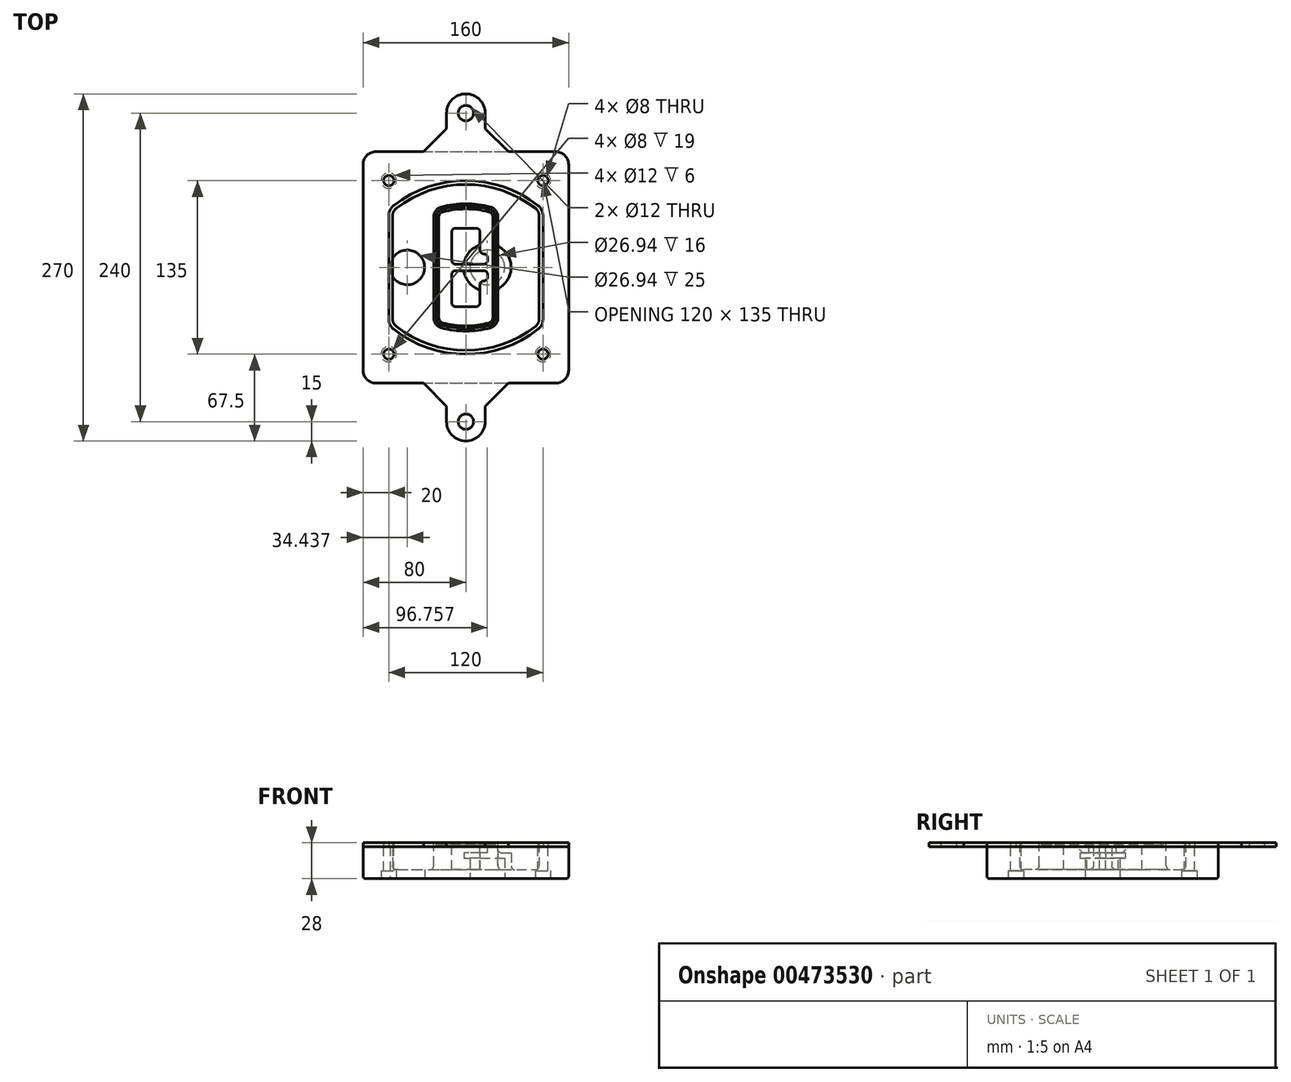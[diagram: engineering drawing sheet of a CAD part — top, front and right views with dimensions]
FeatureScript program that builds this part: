
annotation { "Feature Type Name" : "Feature", "Feature Type Description" : "" }
export const myFeature = defineFeature(function(context is Context, id is Id, definition is map)
    precondition{}
    {
        {
            var Q0;
            Q0=qCreatedBy(makeId("Top.planeOp"),FACE);
            var sketch = newSketch(context, id + "F0", { "sketchPlane" : qUnion([Q0])});
            skPoint(sketch, "E0.rect.middle", {"position": v(0, 0) * mm});
            skLineSegment(sketch, "E1.bottom", {"start": v(-70, -90) * mm, "end": v(70, -90) * mm});
            skLineSegment(sketch, "E1.top", {"start": v(-70, 90) * mm, "end": v(70, 90) * mm});
            skLineSegment(sketch, "E1.left", {"start": v(-80, -80) * mm, "end": v(-80, 80) * mm});
            skLineSegment(sketch, "E1.right", {"start": v(80, -80) * mm, "end": v(80, 80) * mm});
            skLineSegment(sketch, "E2", {"start": v(-80, 90) * mm, "end": v(80, -90) * mm, "construction": true});
            skLineSegment(sketch, "E3", {"start": v(80, 90) * mm, "end": v(-80, -90) * mm, "construction": true});
            skCircle(sketch, "E4", {"center": v(-60, 67.5) * mm, "radius": 4 * mm});
            skCircle(sketch, "E5", {"center": v(60, 67.5) * mm, "radius": 4 * mm});
            skCircle(sketch, "E6", {"center": v(60, -67.5) * mm, "radius": 4 * mm});
            skCircle(sketch, "E7", {"center": v(-60, -67.5) * mm, "radius": 4 * mm});
            skLineSegment(sketch, "E8", {"start": v(-60, 67.5) * mm, "end": v(60, 67.5) * mm, "construction": true});
            skLineSegment(sketch, "E9", {"start": v(60, 67.5) * mm, "end": v(60, -67.5) * mm, "construction": true});
            skLineSegment(sketch, "E10", {"start": v(60, -67.5) * mm, "end": v(-60, -67.5) * mm, "construction": true});
            skLineSegment(sketch, "E11", {"start": v(-60, -67.5) * mm, "end": v(-60, 67.5) * mm, "construction": true});
            skLineSegment(sketch, "E12", {"start": v(-60, 40.3) * mm, "end": v(-60, -40.3) * mm});
            skLineSegment(sketch, "E13", {"start": v(60, 40.3) * mm, "end": v(60, -40.3) * mm});
            skArc(sketch, "E14", {"start": v(56.15, 48.18) * mm, "mid": v(0, 67.5) * mm, "end": v(-56.15, 48.18) * mm});
            skArc(sketch, "E15", {"start": v(-56.15, -48.18) * mm, "mid": v(0, -67.5) * mm, "end": v(56.15, -48.18) * mm});
            skLineSegment(sketch, "E16", {"start": v(-60, 0) * mm, "end": v(60, 0) * mm, "construction": true});
            skPoint(sketch, "E17.visualSharp", {"position": v(-60, -45) * mm});
            skArc(sketch, "E17.filletArc", {"start": v(-60, -40.3) * mm, "mid": v(-58.99, -44.68) * mm, "end": v(-56.15, -48.18) * mm});
            skPoint(sketch, "E18.visualSharp", {"position": v(-60, 45) * mm});
            skArc(sketch, "E18.filletArc", {"start": v(-56.15, 48.18) * mm, "mid": v(-58.99, 44.68) * mm, "end": v(-60, 40.3) * mm});
            skPoint(sketch, "E19.visualSharp", {"position": v(60, 45) * mm});
            skArc(sketch, "E19.filletArc", {"start": v(60, 40.3) * mm, "mid": v(58.99, 44.68) * mm, "end": v(56.15, 48.18) * mm});
            skPoint(sketch, "E20.visualSharp", {"position": v(60, -45) * mm});
            skArc(sketch, "E20.filletArc", {"start": v(56.15, -48.18) * mm, "mid": v(58.99, -44.68) * mm, "end": v(60, -40.3) * mm});
            skPoint(sketch, "E21.visualSharp", {"position": v(-80, 90) * mm});
            skArc(sketch, "E21.filletArc", {"start": v(-70, 90) * mm, "mid": v(-77.07, 87.07) * mm, "end": v(-80, 80) * mm});
            skPoint(sketch, "E22.visualSharp", {"position": v(80, 90) * mm});
            skArc(sketch, "E22.filletArc", {"start": v(80, 80) * mm, "mid": v(77.07, 87.07) * mm, "end": v(70, 90) * mm});
            skPoint(sketch, "E23.visualSharp", {"position": v(80, -90) * mm});
            skArc(sketch, "E23.filletArc", {"start": v(70, -90) * mm, "mid": v(77.07, -87.07) * mm, "end": v(80, -80) * mm});
            skPoint(sketch, "E24.visualSharp", {"position": v(-80, -90) * mm});
            skArc(sketch, "E24.filletArc", {"start": v(-80, -80) * mm, "mid": v(-77.07, -87.07) * mm, "end": v(-70, -90) * mm});
            skArc(sketch, "E25.0", {"start": v(57, 40.3) * mm, "mid": v(56.3, 43.36) * mm, "end": v(54.3, 45.81) * mm});
            skLineSegment(sketch, "E25.1", {"start": v(57, 40.3) * mm, "end": v(57, -40.3) * mm});
            skArc(sketch, "E25.2", {"start": v(54.3, -45.81) * mm, "mid": v(56.3, -43.36) * mm, "end": v(57, -40.3) * mm});
            skArc(sketch, "E25.3", {"start": v(-54.3, -45.81) * mm, "mid": v(0, -64.5) * mm, "end": v(54.3, -45.81) * mm});
            skArc(sketch, "E25.4", {"start": v(-57, -40.3) * mm, "mid": v(-56.3, -43.36) * mm, "end": v(-54.3, -45.81) * mm});
            skArc(sketch, "E25.5", {"start": v(54.3, 45.81) * mm, "mid": v(0, 64.5) * mm, "end": v(-54.3, 45.81) * mm});
            skLineSegment(sketch, "E25.6", {"start": v(-57, 40.3) * mm, "end": v(-57, -40.3) * mm});
            skArc(sketch, "E25.7", {"start": v(-54.3, 45.81) * mm, "mid": v(-56.3, 43.36) * mm, "end": v(-57, 40.3) * mm});
            skArc(sketch, "E26.0", {"start": v(-58.62, 51.33) * mm, "mid": v(-62.58, 46.43) * mm, "end": v(-64, 40.3) * mm});
            skArc(sketch, "E26.1", {"start": v(58.62, 51.33) * mm, "mid": v(0, 71.5) * mm, "end": v(-58.62, 51.33) * mm});
            skArc(sketch, "E26.2", {"start": v(64, 40.3) * mm, "mid": v(62.58, 46.43) * mm, "end": v(58.62, 51.33) * mm});
            skLineSegment(sketch, "E26.3", {"start": v(64, 40.3) * mm, "end": v(64, -40.3) * mm});
            skArc(sketch, "E26.4", {"start": v(58.62, -51.33) * mm, "mid": v(62.58, -46.43) * mm, "end": v(64, -40.3) * mm});
            skLineSegment(sketch, "E26.5", {"start": v(-64, 40.3) * mm, "end": v(-64, -40.3) * mm});
            skArc(sketch, "E26.6", {"start": v(-58.62, -51.33) * mm, "mid": v(0, -71.5) * mm, "end": v(58.62, -51.33) * mm});
            skArc(sketch, "E26.7", {"start": v(-64, -40.3) * mm, "mid": v(-62.58, -46.43) * mm, "end": v(-58.62, -51.33) * mm});
            skSolve(sketch);
        }
        {
            var Q0;
            Q0=makeQuery(id+"F0.imprint","IMPRINT",FACE,{"disambiguationData":[TD([[makeQuery(id+"F0.imprint","IMPRINT",EDGE,{"derivedFrom":sQuery(id+"F0.wireOp",EDGE,"E1.bottom")}),1.0]])]});
            var Q1;
            Q1=makeQuery(id+"F0.imprint","IMPRINT",FACE,{"disambiguationData":[TD([[makeQuery(id+"F0.imprint","IMPRINT",EDGE,{"derivedFrom":sQuery(id+"F0.wireOp",EDGE,"E12")}),1.0]])]});
            var Q2;
            Q2=makeQuery(id+"F0.imprint","IMPRINT",FACE,{"disambiguationData":[TD([[makeQuery(id+"F0.imprint","IMPRINT",EDGE,{"derivedFrom":sQuery(id+"F0.wireOp",EDGE,"E25.0")}),1.0]])]});
            var Q3;
            Q3=makeQuery(id+"F0.imprint","IMPRINT",FACE,{"disambiguationData":[TD([[makeQuery(id+"F0.imprint","IMPRINT",EDGE,{"derivedFrom":sQuery(id+"F0.wireOp",EDGE,"E12")}),-1.0]])]});
            extrude(context, id + "F1", {"entities" : qUnion([Q0, Q1, Q2, Q3]), "oppositeDirection" : true, "depth" : 25 * mm});
        }
        {
            var Q0;
            Q0=makeQuery(id+"F0.imprint","IMPRINT",FACE,{"disambiguationData":[TD([[makeQuery(id+"F0.imprint","IMPRINT",EDGE,{"derivedFrom":sQuery(id+"F0.wireOp",EDGE,"E12")}),1.0]])]});
            extrude(context, id + "F2", {"entities" : qUnion([Q0]), "operationType" : NewBodyOperationType.ADD, "depth" : 3 * mm});
        }
        {
            var Q0;
            Q0=makeQuery(id+"F0.imprint","IMPRINT",FACE,{"disambiguationData":[TD([[makeQuery(id+"F0.imprint","IMPRINT",EDGE,{"derivedFrom":sQuery(id+"F0.wireOp",EDGE,"E25.0")}),1.0]])]});
            extrude(context, id + "F3", {"entities" : qUnion([Q0]), "operationType" : NewBodyOperationType.REMOVE, "oppositeDirection" : true, "depth" : 18 * mm});
        }
        {
            var Q0;
            Q0=makeQuery(id+"F2.opExtrude","CAP_FACE",FACE,{"disambiguationData":[OSD([sQuery(id+"F0.wireOp",EDGE,"E12"),sQuery(id+"F0.wireOp",EDGE,"E13"),sQuery(id+"F0.wireOp",EDGE,"E14"),sQuery(id+"F0.wireOp",EDGE,"E15"),sQuery(id+"F0.wireOp",EDGE,"E17.filletArc"),sQuery(id+"F0.wireOp",EDGE,"E18.filletArc"),sQuery(id+"F0.wireOp",EDGE,"E19.filletArc"),sQuery(id+"F0.wireOp",EDGE,"E20.filletArc"),sQuery(id+"F0.wireOp",EDGE,"E25.0"),sQuery(id+"F0.wireOp",EDGE,"E25.1"),sQuery(id+"F0.wireOp",EDGE,"E25.2"),sQuery(id+"F0.wireOp",EDGE,"E25.3"),sQuery(id+"F0.wireOp",EDGE,"E25.4"),sQuery(id+"F0.wireOp",EDGE,"E25.5"),sQuery(id+"F0.wireOp",EDGE,"E25.6"),sQuery(id+"F0.wireOp",EDGE,"E25.7")])],"isStart":false});
            var sketch = newSketch(context, id + "F4", { "sketchPlane" : qUnion([Q0])});
            skArc(sketch, "E27.0", {"start": v(-19.08, -46.97) * mm, "mid": v(0, -49.5) * mm, "end": v(19.08, -46.97) * mm});
            skArc(sketch, "E28.0", {"start": v(19.08, 46.97) * mm, "mid": v(0, 49.5) * mm, "end": v(-19.08, 46.97) * mm});
            skLineSegment(sketch, "E29", {"start": v(-25, 39.25) * mm, "end": v(-25, -39.25) * mm});
            skLineSegment(sketch, "E30", {"start": v(25, 39.25) * mm, "end": v(25, -39.25) * mm});
            skLineSegment(sketch, "E31", {"start": v(-25, 45.1) * mm, "end": v(25, 45.1) * mm, "construction": true});
            skLineSegment(sketch, "E32", {"start": v(-25, -45.1) * mm, "end": v(25, -45.1) * mm, "construction": true});
            skPoint(sketch, "E33.visualSharp", {"position": v(-25, 45.1) * mm});
            skArc(sketch, "E33.filletArc", {"start": v(-19.08, 46.97) * mm, "mid": v(-23.35, 44.11) * mm, "end": v(-25, 39.25) * mm});
            skPoint(sketch, "E34.visualSharp", {"position": v(25, 45.1) * mm});
            skArc(sketch, "E34.filletArc", {"start": v(25, 39.25) * mm, "mid": v(23.35, 44.11) * mm, "end": v(19.08, 46.97) * mm});
            skPoint(sketch, "E35.visualSharp", {"position": v(25, -45.1) * mm});
            skArc(sketch, "E35.filletArc", {"start": v(19.08, -46.97) * mm, "mid": v(23.35, -44.11) * mm, "end": v(25, -39.25) * mm});
            skPoint(sketch, "E36.visualSharp", {"position": v(-25, -45.1) * mm});
            skArc(sketch, "E36.filletArc", {"start": v(-25, -39.25) * mm, "mid": v(-23.35, -44.11) * mm, "end": v(-19.08, -46.97) * mm});
            skArc(sketch, "E37.0", {"start": v(54.3, 45.81) * mm, "mid": v(0, 64.5) * mm, "end": v(-54.3, 45.81) * mm});
            skArc(sketch, "E37.1", {"start": v(-54.3, 45.81) * mm, "mid": v(-56.3, 43.36) * mm, "end": v(-57, 40.3) * mm});
            skLineSegment(sketch, "E37.2", {"start": v(-57, 40.3) * mm, "end": v(-57, -40.3) * mm});
            skArc(sketch, "E37.3", {"start": v(-57, -40.3) * mm, "mid": v(-56.3, -43.36) * mm, "end": v(-54.3, -45.81) * mm});
            skArc(sketch, "E37.4", {"start": v(-54.3, -45.81) * mm, "mid": v(0, -64.5) * mm, "end": v(54.3, -45.81) * mm});
            skArc(sketch, "E37.5", {"start": v(54.3, -45.81) * mm, "mid": v(56.3, -43.36) * mm, "end": v(57, -40.3) * mm});
            skLineSegment(sketch, "E37.6", {"start": v(57, 40.3) * mm, "end": v(57, -40.3) * mm});
            skArc(sketch, "E37.7", {"start": v(57, 40.3) * mm, "mid": v(56.3, 43.36) * mm, "end": v(54.3, 45.81) * mm});
            skLineSegment(sketch, "E38.0", {"start": v(23, 39.25) * mm, "end": v(23, -39.25) * mm});
            skArc(sketch, "E38.1", {"start": v(18.56, -45.04) * mm, "mid": v(21.76, -42.9) * mm, "end": v(23, -39.25) * mm});
            skArc(sketch, "E38.2", {"start": v(-18.56, -45.04) * mm, "mid": v(0, -47.5) * mm, "end": v(18.56, -45.04) * mm});
            skArc(sketch, "E38.3", {"start": v(-23, -39.25) * mm, "mid": v(-21.76, -42.9) * mm, "end": v(-18.56, -45.04) * mm});
            skLineSegment(sketch, "E38.4", {"start": v(-23, 39.25) * mm, "end": v(-23, -39.25) * mm});
            skArc(sketch, "E38.5", {"start": v(23, 39.25) * mm, "mid": v(21.76, 42.9) * mm, "end": v(18.56, 45.04) * mm});
            skArc(sketch, "E38.6", {"start": v(-18.56, 45.04) * mm, "mid": v(-21.76, 42.9) * mm, "end": v(-23, 39.25) * mm});
            skArc(sketch, "E38.7", {"start": v(18.56, 45.04) * mm, "mid": v(0, 47.5) * mm, "end": v(-18.56, 45.04) * mm});
            skArc(sketch, "E39.0", {"start": v(21, 39.25) * mm, "mid": v(20.18, 41.68) * mm, "end": v(18.04, 43.1) * mm});
            skLineSegment(sketch, "E39.1", {"start": v(21, 39.25) * mm, "end": v(21, -39.25) * mm});
            skArc(sketch, "E39.2", {"start": v(18.04, -43.1) * mm, "mid": v(20.18, -41.68) * mm, "end": v(21, -39.25) * mm});
            skArc(sketch, "E39.3", {"start": v(-18.04, -43.1) * mm, "mid": v(0, -45.5) * mm, "end": v(18.04, -43.1) * mm});
            skArc(sketch, "E39.4", {"start": v(-21, -39.25) * mm, "mid": v(-20.18, -41.68) * mm, "end": v(-18.04, -43.1) * mm});
            skArc(sketch, "E39.5", {"start": v(18.04, 43.1) * mm, "mid": v(0, 45.5) * mm, "end": v(-18.04, 43.1) * mm});
            skLineSegment(sketch, "E39.6", {"start": v(-21, 39.25) * mm, "end": v(-21, -39.25) * mm});
            skArc(sketch, "E39.7", {"start": v(-18.04, 43.1) * mm, "mid": v(-20.18, 41.68) * mm, "end": v(-21, 39.25) * mm});
            skLineSegment(sketch, "E40", {"start": v(-25, 0) * mm, "end": v(25, 0) * mm, "construction": true});
            skLineSegment(sketch, "E41", {"start": v(-11, 5.5) * mm, "end": v(-11, 27.5) * mm});
            skLineSegment(sketch, "E42", {"start": v(-8, 30.5) * mm, "end": v(8, 30.5) * mm});
            skLineSegment(sketch, "E43", {"start": v(11, 27.5) * mm, "end": v(11, 13.5) * mm});
            skLineSegment(sketch, "E44", {"start": v(14, 10.5) * mm, "end": v(14, 10.5) * mm});
            skLineSegment(sketch, "E45", {"start": v(17, 7.5) * mm, "end": v(17, 5.5) * mm});
            skLineSegment(sketch, "E46", {"start": v(14, 2.5) * mm, "end": v(-8, 2.5) * mm});
            skPoint(sketch, "E47.visualSharp", {"position": v(-11, 30.5) * mm});
            skArc(sketch, "E47.filletArc", {"start": v(-8, 30.5) * mm, "mid": v(-10.12, 29.62) * mm, "end": v(-11, 27.5) * mm});
            skPoint(sketch, "E48.visualSharp", {"position": v(11, 30.5) * mm});
            skArc(sketch, "E48.filletArc", {"start": v(11, 27.5) * mm, "mid": v(10.12, 29.62) * mm, "end": v(8, 30.5) * mm});
            skPoint(sketch, "E49.visualSharp", {"position": v(11, 10.5) * mm});
            skArc(sketch, "E49.filletArc", {"start": v(11, 13.5) * mm, "mid": v(11.88, 11.38) * mm, "end": v(14, 10.5) * mm});
            skPoint(sketch, "E50.visualSharp", {"position": v(17, 10.5) * mm});
            skArc(sketch, "E50.filletArc", {"start": v(17, 7.5) * mm, "mid": v(16.12, 9.62) * mm, "end": v(14, 10.5) * mm});
            skPoint(sketch, "E51.visualSharp", {"position": v(17, 2.5) * mm});
            skArc(sketch, "E51.filletArc", {"start": v(14, 2.5) * mm, "mid": v(16.12, 3.38) * mm, "end": v(17, 5.5) * mm});
            skPoint(sketch, "E52.visualSharp", {"position": v(-11, 2.5) * mm});
            skArc(sketch, "E52.filletArc", {"start": v(-11, 5.5) * mm, "mid": v(-10.12, 3.38) * mm, "end": v(-8, 2.5) * mm});
            skLineSegment(sketch, "E53.0.MirrorCS", {"start": v(14, -2.5) * mm, "end": v(-8, -2.5) * mm});
            skArc(sketch, "E54.0.MirrorCS", {"start": v(-11, -5.5) * mm, "mid": v(-10.12, -3.38) * mm, "end": v(-8, -2.5) * mm});
            skLineSegment(sketch, "E55.0.MirrorCS", {"start": v(-11, -5.5) * mm, "end": v(-11, -27.5) * mm});
            skArc(sketch, "E56.0.MirrorCS", {"start": v(-8, -30.5) * mm, "mid": v(-10.12, -29.62) * mm, "end": v(-11, -27.5) * mm});
            skLineSegment(sketch, "E57.0.MirrorCS", {"start": v(-8, -30.5) * mm, "end": v(8, -30.5) * mm});
            skArc(sketch, "E58.0.MirrorCS", {"start": v(11, -27.5) * mm, "mid": v(10.12, -29.62) * mm, "end": v(8, -30.5) * mm});
            skLineSegment(sketch, "E59.0.MirrorCS", {"start": v(11, -27.5) * mm, "end": v(11, -13.5) * mm});
            skArc(sketch, "E60.0.MirrorCS", {"start": v(11, -13.5) * mm, "mid": v(11.88, -11.38) * mm, "end": v(14, -10.5) * mm});
            skArc(sketch, "E61.0.MirrorCS", {"start": v(17, -7.5) * mm, "mid": v(16.12, -9.62) * mm, "end": v(14, -10.5) * mm});
            skLineSegment(sketch, "E62.0.MirrorCS", {"start": v(17, -7.5) * mm, "end": v(17, -5.5) * mm});
            skArc(sketch, "E63.0.MirrorCS", {"start": v(14, -2.5) * mm, "mid": v(16.12, -3.38) * mm, "end": v(17, -5.5) * mm});
            skSolve(sketch);
        }
        {
            var Q0;
            Q0=makeQuery(id+"F4.imprint","IMPRINT",FACE,{"disambiguationData":[TD([[makeQuery(id+"F4.imprint","IMPRINT",EDGE,{"derivedFrom":sQuery(id+"F4.wireOp",EDGE,"E27.0")}),1.0]])]});
            var Q1;
            Q1=makeQuery(id+"F4.imprint","IMPRINT",FACE,{"disambiguationData":[TD([[makeQuery(id+"F4.imprint","IMPRINT",EDGE,{"derivedFrom":sQuery(id+"F4.wireOp",EDGE,"E38.0")}),-1.0]])]});
            var Q2;
            Q2=makeQuery(id+"F4.imprint","IMPRINT",FACE,{"disambiguationData":[TD([[makeQuery(id+"F4.imprint","IMPRINT",EDGE,{"derivedFrom":sQuery(id+"F4.wireOp",EDGE,"E39.0")}),1.0]])]});
            extrude(context, id + "F5", {"entities" : qUnion([Q0, Q1, Q2]), "operationType" : NewBodyOperationType.ADD, "endBound" : BoundingType.UP_TO_NEXT, "oppositeDirection" : true, "depth" : 25 * mm});
        }
        {
            var Q0;
            Q0=makeQuery(id+"F4.imprint","IMPRINT",FACE,{"disambiguationData":[TD([[makeQuery(id+"F4.imprint","IMPRINT",EDGE,{"derivedFrom":sQuery(id+"F4.wireOp",EDGE,"E38.0")}),-1.0]])]});
            extrude(context, id + "F6", {"entities" : qUnion([Q0]), "operationType" : NewBodyOperationType.REMOVE, "oppositeDirection" : true, "depth" : 2 * mm});
        }
        {
            var Q0;
            Q0=makeQuery(id+"F1.opExtrude","CAP_FACE",FACE,{"disambiguationData":[OSD([sQuery(id+"F0.wireOp",EDGE,"E1.bottom"),sQuery(id+"F0.wireOp",EDGE,"E1.top"),sQuery(id+"F0.wireOp",EDGE,"E1.left"),sQuery(id+"F0.wireOp",EDGE,"E1.right"),sQuery(id+"F0.wireOp",EDGE,"E4"),sQuery(id+"F0.wireOp",EDGE,"E5"),sQuery(id+"F0.wireOp",EDGE,"E6"),sQuery(id+"F0.wireOp",EDGE,"E7"),sQuery(id+"F0.wireOp",EDGE,"E21.filletArc"),sQuery(id+"F0.wireOp",EDGE,"E22.filletArc"),sQuery(id+"F0.wireOp",EDGE,"E23.filletArc"),sQuery(id+"F0.wireOp",EDGE,"E24.filletArc")])],"isStart":false});
            var sketch = newSketch(context, id + "F7", { "sketchPlane" : qUnion([Q0])});
            skCircle(sketch, "E64", {"center": v(16.76, 0) * mm, "radius": 13.47 * mm});
            skCircle(sketch, "E65", {"center": v(-45.56, 0) * mm, "radius": 13.47 * mm});
            skLineSegment(sketch, "E66", {"start": v(80, 0) * mm, "end": v(-80, 0) * mm});
            skCircle(sketch, "E67", {"center": v(16.76, 0) * mm, "radius": 18.47 * mm});
            skCircle(sketch, "E68", {"center": v(60, -67.5) * mm, "radius": 6 * mm});
            skCircle(sketch, "E69", {"center": v(-60, -67.5) * mm, "radius": 6 * mm});
            skCircle(sketch, "E70", {"center": v(-60, 67.5) * mm, "radius": 6 * mm});
            skCircle(sketch, "E71", {"center": v(60, 67.5) * mm, "radius": 6 * mm});
            skSolve(sketch);
        }
        {
            var Q0;
            {var subQ1=sQuery(id+"F7.wireOp",EDGE,"E66");var subQ4=sQuery(id+"F7.wireOp",EDGE,"E64");var subQ6=makeQuery(id+"F7.imprint","INTERSECT",VERTEX,{"disambiguationData":[OD(0.0)],"derivedFrom":[subQ4,subQ1]});Q0=makeQuery(id+"F7.imprint","IMPRINT",FACE,{"disambiguationData":[TD([[makeQuery(id+"F7.imprint","IMPRINT",EDGE,{"disambiguationData":[TD([[subQ6,-1.0]])],"derivedFrom":subQ4}),-1.0]])]});}
            var Q1;
            {var subQ0=sQuery(id+"F7.wireOp",EDGE,"E66");var subQ1=sQuery(id+"F7.wireOp",EDGE,"E64");var subQ3=makeQuery(id+"F7.imprint","INTERSECT",VERTEX,{"disambiguationData":[OD(0.0)],"derivedFrom":[subQ1,subQ0]});Q1=makeQuery(id+"F7.imprint","IMPRINT",FACE,{"disambiguationData":[TD([[makeQuery(id+"F7.imprint","IMPRINT",EDGE,{"disambiguationData":[TD([[subQ3,-1.0]])],"derivedFrom":subQ1}),1.0]])]});}
            var Q2;
            {var subQ0=sQuery(id+"F7.wireOp",EDGE,"E66");var subQ1=sQuery(id+"F7.wireOp",EDGE,"E64");var subQ3=makeQuery(id+"F7.imprint","INTERSECT",VERTEX,{"disambiguationData":[OD(0.0)],"derivedFrom":[subQ1,subQ0]});Q2=makeQuery(id+"F7.imprint","IMPRINT",FACE,{"disambiguationData":[TD([[makeQuery(id+"F7.imprint","IMPRINT",EDGE,{"disambiguationData":[TD([[subQ3,1.0]])],"derivedFrom":subQ1}),1.0]])]});}
            var Q3;
            {var subQ1=sQuery(id+"F7.wireOp",EDGE,"E66");var subQ4=sQuery(id+"F7.wireOp",EDGE,"E64");var subQ6=makeQuery(id+"F7.imprint","INTERSECT",VERTEX,{"disambiguationData":[OD(0.0)],"derivedFrom":[subQ4,subQ1]});Q3=makeQuery(id+"F7.imprint","IMPRINT",FACE,{"disambiguationData":[TD([[makeQuery(id+"F7.imprint","IMPRINT",EDGE,{"disambiguationData":[TD([[subQ6,1.0]])],"derivedFrom":subQ4}),-1.0]])]});}
            extrude(context, id + "F8", {"entities" : qUnion([Q0, Q1, Q2, Q3]), "operationType" : NewBodyOperationType.ADD, "oppositeDirection" : true, "depth" : 20 * mm});
        }
        {
            var Q0;
            {var subQ0=sQuery(id+"F7.wireOp",EDGE,"E66");var subQ1=sQuery(id+"F7.wireOp",EDGE,"E64");var subQ3=makeQuery(id+"F7.imprint","INTERSECT",VERTEX,{"disambiguationData":[OD(0.0)],"derivedFrom":[subQ1,subQ0]});Q0=makeQuery(id+"F7.imprint","IMPRINT",FACE,{"disambiguationData":[TD([[makeQuery(id+"F7.imprint","IMPRINT",EDGE,{"disambiguationData":[TD([[subQ3,-1.0]])],"derivedFrom":subQ1}),1.0]])]});}
            var Q1;
            {var subQ0=sQuery(id+"F7.wireOp",EDGE,"E66");var subQ1=sQuery(id+"F7.wireOp",EDGE,"E64");var subQ3=makeQuery(id+"F7.imprint","INTERSECT",VERTEX,{"disambiguationData":[OD(0.0)],"derivedFrom":[subQ1,subQ0]});Q1=makeQuery(id+"F7.imprint","IMPRINT",FACE,{"disambiguationData":[TD([[makeQuery(id+"F7.imprint","IMPRINT",EDGE,{"disambiguationData":[TD([[subQ3,1.0]])],"derivedFrom":subQ1}),1.0]])]});}
            extrude(context, id + "F9", {"entities" : qUnion([Q0, Q1]), "operationType" : NewBodyOperationType.REMOVE, "oppositeDirection" : true, "depth" : 16 * mm});
        }
        {
            var Q0;
            {var subQ0=sQuery(id+"F7.wireOp",EDGE,"E66");var subQ1=sQuery(id+"F7.wireOp",EDGE,"E65");var subQ3=makeQuery(id+"F7.imprint","INTERSECT",VERTEX,{"disambiguationData":[OD(0.0)],"derivedFrom":[subQ1,subQ0]});Q0=makeQuery(id+"F7.imprint","IMPRINT",FACE,{"disambiguationData":[TD([[makeQuery(id+"F7.imprint","IMPRINT",EDGE,{"disambiguationData":[TD([[subQ3,-1.0]])],"derivedFrom":subQ1}),1.0]])]});}
            var Q1;
            {var subQ0=sQuery(id+"F7.wireOp",EDGE,"E66");var subQ1=sQuery(id+"F7.wireOp",EDGE,"E65");var subQ3=makeQuery(id+"F7.imprint","INTERSECT",VERTEX,{"disambiguationData":[OD(0.0)],"derivedFrom":[subQ1,subQ0]});Q1=makeQuery(id+"F7.imprint","IMPRINT",FACE,{"disambiguationData":[TD([[makeQuery(id+"F7.imprint","IMPRINT",EDGE,{"disambiguationData":[TD([[subQ3,1.0]])],"derivedFrom":subQ1}),1.0]])]});}
            extrude(context, id + "F10", {"entities" : qUnion([Q0, Q1]), "operationType" : NewBodyOperationType.REMOVE, "oppositeDirection" : true, "depth" : 25 * mm});
        }
        {
            var Q0;
            Q0=makeQuery(id+"F7.imprint","IMPRINT",FACE,{"disambiguationData":[TD([[makeQuery(id+"F7.imprint","IMPRINT",EDGE,{"derivedFrom":sQuery(id+"F7.wireOp",EDGE,"E68")}),1.0]])]});
            var Q1;
            Q1=makeQuery(id+"F7.imprint","IMPRINT",FACE,{"disambiguationData":[TD([[makeQuery(id+"F7.imprint","IMPRINT",EDGE,{"derivedFrom":makeQuery(id+"F1.opExtrude","CAP_EDGE",EDGE,{"disambiguationData":[OSD([sQuery(id+"F0.wireOp",EDGE,"E5")])],"isStart":false})}),-1.0]])]});
            var Q2;
            Q2=makeQuery(id+"F7.imprint","IMPRINT",FACE,{"disambiguationData":[TD([[makeQuery(id+"F7.imprint","IMPRINT",EDGE,{"derivedFrom":sQuery(id+"F7.wireOp",EDGE,"E69")}),1.0]])]});
            var Q3;
            Q3=makeQuery(id+"F7.imprint","IMPRINT",FACE,{"disambiguationData":[TD([[makeQuery(id+"F7.imprint","IMPRINT",EDGE,{"derivedFrom":makeQuery(id+"F1.opExtrude","CAP_EDGE",EDGE,{"disambiguationData":[OSD([sQuery(id+"F0.wireOp",EDGE,"E4")])],"isStart":false})}),-1.0]])]});
            var Q4;
            Q4=makeQuery(id+"F7.imprint","IMPRINT",FACE,{"disambiguationData":[TD([[makeQuery(id+"F7.imprint","IMPRINT",EDGE,{"derivedFrom":sQuery(id+"F7.wireOp",EDGE,"E70")}),1.0]])]});
            var Q5;
            Q5=makeQuery(id+"F7.imprint","IMPRINT",FACE,{"disambiguationData":[TD([[makeQuery(id+"F7.imprint","IMPRINT",EDGE,{"derivedFrom":makeQuery(id+"F1.opExtrude","CAP_EDGE",EDGE,{"disambiguationData":[OSD([sQuery(id+"F0.wireOp",EDGE,"E7")])],"isStart":false})}),-1.0]])]});
            var Q6;
            Q6=makeQuery(id+"F7.imprint","IMPRINT",FACE,{"disambiguationData":[TD([[makeQuery(id+"F7.imprint","IMPRINT",EDGE,{"derivedFrom":sQuery(id+"F7.wireOp",EDGE,"E71")}),1.0]])]});
            var Q7;
            Q7=makeQuery(id+"F7.imprint","IMPRINT",FACE,{"disambiguationData":[TD([[makeQuery(id+"F7.imprint","IMPRINT",EDGE,{"derivedFrom":makeQuery(id+"F1.opExtrude","CAP_EDGE",EDGE,{"disambiguationData":[OSD([sQuery(id+"F0.wireOp",EDGE,"E6")])],"isStart":false})}),-1.0]])]});
            extrude(context, id + "F11", {"entities" : qUnion([Q0, Q1, Q2, Q3, Q4, Q5, Q6, Q7]), "operationType" : NewBodyOperationType.REMOVE, "oppositeDirection" : true, "depth" : 6 * mm});
        }
        {
            var Q0;
            Q0=makeQuery(id+"F9.boolean.opBoolean","COPY",FACE,{"derivedFrom":makeQuery(id+"F9.opExtrude","CAP_FACE",FACE,{"disambiguationData":[OSD([sQuery(id+"F7.wireOp",EDGE,"E64")])],"isStart":false})});
            var sketch = newSketch(context, id + "F12", { "sketchPlane" : qUnion([Q0])});
            skArc(sketch, "E72.0", {"start": v(11, 17.55) * mm, "mid": v(2.57, 11.82) * mm, "end": v(-1.54, 2.5) * mm});
            skArc(sketch, "E72.1", {"start": v(-1.54, -2.5) * mm, "mid": v(2.57, -11.82) * mm, "end": v(11, -17.55) * mm});
            skLineSegment(sketch, "E73", {"start": v(-1.54, -2.5) * mm, "end": v(14, -2.5) * mm});
            skLineSegment(sketch, "E74.0", {"start": v(14, 2.5) * mm, "end": v(-1.54, 2.5) * mm});
            skArc(sketch, "E74.1", {"start": v(14, 2.5) * mm, "mid": v(16.12, 3.38) * mm, "end": v(17, 5.5) * mm});
            skLineSegment(sketch, "E74.2", {"start": v(17, 7.5) * mm, "end": v(17, 5.5) * mm});
            skArc(sketch, "E74.3", {"start": v(17, 7.5) * mm, "mid": v(16.12, 9.62) * mm, "end": v(14, 10.5) * mm});
            skArc(sketch, "E74.4", {"start": v(11, 13.5) * mm, "mid": v(11.88, 11.38) * mm, "end": v(14, 10.5) * mm});
            skLineSegment(sketch, "E74.5", {"start": v(11, 17.55) * mm, "end": v(11, 13.5) * mm});
            skLineSegment(sketch, "E74.7", {"start": v(14, -2.5) * mm, "end": v(-1.54, -2.5) * mm});
            skArc(sketch, "E74.8", {"start": v(14, -2.5) * mm, "mid": v(16.12, -3.38) * mm, "end": v(17, -5.5) * mm});
            skLineSegment(sketch, "E74.9", {"start": v(17, -7.5) * mm, "end": v(17, -5.5) * mm});
            skArc(sketch, "E74.10", {"start": v(17, -7.5) * mm, "mid": v(16.12, -9.62) * mm, "end": v(14, -10.5) * mm});
            skArc(sketch, "E74.11", {"start": v(11, -13.5) * mm, "mid": v(11.88, -11.38) * mm, "end": v(14, -10.5) * mm});
            skLineSegment(sketch, "E74.12", {"start": v(11, -17.55) * mm, "end": v(11, -13.5) * mm});
            skPoint(sketch, "E75.orphan", {"position": v(11, -27.5) * mm});
            skPoint(sketch, "E76.orphan", {"position": v(-8, -2.5) * mm});
            skPoint(sketch, "E77.orphan", {"position": v(-8, 2.5) * mm});
            skPoint(sketch, "E78.orphan", {"position": v(11, 27.5) * mm});
            skSolve(sketch);
        }
        {
            var Q0;
            {var subQ7=sQuery(id+"F12.wireOp",EDGE,"E72.0");var subQ14=sQuery(id+"F12.wireOp",EDGE,"E72.1");var subQ16=sQuery(id+"F12.wireOp",EDGE,"E74.1");var subQ18=sQuery(id+"F12.wireOp",EDGE,"E74.8");Q0=qUnion([makeQuery(id+"F12.imprint","IMPRINT",FACE,{"disambiguationData":[TD([[makeQuery(id+"F12.imprint","IMPRINT",EDGE,{"derivedFrom":subQ7}),1.0]])]}),makeQuery(id+"F12.imprint","IMPRINT",FACE,{"disambiguationData":[TD([[makeQuery(id+"F12.imprint","IMPRINT",EDGE,{"derivedFrom":subQ14}),1.0]])]}),makeQuery(id+"F12.imprint","IMPRINT",FACE,{"disambiguationData":[TD([[makeQuery(id+"F12.imprint","IMPRINT",EDGE,{"derivedFrom":subQ16}),1.0]])]}),makeQuery(id+"F12.imprint","IMPRINT",FACE,{"disambiguationData":[TD([[makeQuery(id+"F12.imprint","IMPRINT",EDGE,{"derivedFrom":subQ18}),-1.0]])]})]);}
            var Q1;
            Q1=makeQuery(id+"F5.boolean.opBoolean","SPLIT",FACE,{"disambiguationData":[TD([makeQuery(id+"F5.opExtrude","SWEPT_FACE",FACE,{"disambiguationData":[OSD([sQuery(id+"F4.wireOp",EDGE,"E41")])]})])],"derivedFrom":makeQuery(id+"F3.boolean.opBoolean","COPY",FACE,{"derivedFrom":makeQuery(id+"F3.opExtrude","CAP_FACE",FACE,{"disambiguationData":[OSD([sQuery(id+"F0.wireOp",EDGE,"E25.0"),sQuery(id+"F0.wireOp",EDGE,"E25.1"),sQuery(id+"F0.wireOp",EDGE,"E25.2"),sQuery(id+"F0.wireOp",EDGE,"E25.3"),sQuery(id+"F0.wireOp",EDGE,"E25.4"),sQuery(id+"F0.wireOp",EDGE,"E25.5"),sQuery(id+"F0.wireOp",EDGE,"E25.6"),sQuery(id+"F0.wireOp",EDGE,"E25.7")])],"isStart":false})})});
            extrude(context, id + "F13", {"entities" : qUnion([Q0]), "operationType" : NewBodyOperationType.REMOVE, "endBound" : BoundingType.UP_TO_SURFACE, "endBoundEntityFace" : qUnion([Q1]), "depth" : 25 * mm});
        }
        {
            var Q0;
            Q0=makeQuery(id+"F3.boolean.opBoolean","COPY",EDGE,{"derivedFrom":makeQuery(id+"F3.opExtrude","CAP_EDGE",EDGE,{"disambiguationData":[OSD([sQuery(id+"F0.wireOp",EDGE,"E25.6")])],"isStart":false})});
            var Q1;
            Q1=makeQuery(id+"F8.boolean.opBoolean","INTERSECT",EDGE,{"derivedFrom":[makeQuery(id+"F5.opExtrude","SWEPT_FACE",FACE,{"disambiguationData":[OSD([sQuery(id+"F4.wireOp",EDGE,"E30")])]}),makeQuery(id+"F8.opExtrude","CAP_FACE",FACE,{"disambiguationData":[OSD([sQuery(id+"F7.wireOp",EDGE,"E67")])],"isStart":false})]});
            var Q2;
            Q2=makeQuery(id+"F8.boolean.opBoolean","INTERSECT",EDGE,{"disambiguationData":[OD(1.0)],"derivedFrom":[makeQuery(id+"F5.opExtrude","SWEPT_FACE",FACE,{"disambiguationData":[OSD([sQuery(id+"F4.wireOp",EDGE,"E30")])]}),makeQuery(id+"F8.opExtrude","SWEPT_FACE",FACE,{"disambiguationData":[OSD([sQuery(id+"F7.wireOp",EDGE,"E67")])]})]});
            var Q3;
            {var subQ0=sQuery(id+"F4.wireOp",EDGE,"E30");Q3=makeQuery(id+"F8.boolean.opBoolean","SPLIT",EDGE,{"disambiguationData":[TD([makeQuery(id+"F5.opExtrude","SWEPT_FACE",FACE,{"disambiguationData":[OSD([sQuery(id+"F4.wireOp",EDGE,"E35.filletArc")])]})])],"derivedFrom":makeQuery(id+"F5.opExtrude","CAP_EDGE",EDGE,{"disambiguationData":[OSD([subQ0])],"isStart":false})});}
            var Q4;
            {var subQ0=sQuery(id+"F0.wireOp",EDGE,"E25.7");var subQ1=sQuery(id+"F0.wireOp",EDGE,"E25.1");var subQ2=sQuery(id+"F0.wireOp",EDGE,"E25.6");var subQ3=sQuery(id+"F0.wireOp",EDGE,"E25.5");var subQ4=sQuery(id+"F0.wireOp",EDGE,"E25.4");var subQ5=sQuery(id+"F0.wireOp",EDGE,"E25.0");var subQ6=sQuery(id+"F0.wireOp",EDGE,"E25.2");var subQ7=sQuery(id+"F0.wireOp",EDGE,"E25.3");Q4=makeQuery(id+"F8.boolean.opBoolean","INTERSECT",EDGE,{"derivedFrom":[makeQuery(id+"F5.boolean.opBoolean","SPLIT",FACE,{"disambiguationData":[TD([makeQuery(id+"F2.opExtrude","SWEPT_FACE",FACE,{"disambiguationData":[OSD([subQ5])]})])],"derivedFrom":makeQuery(id+"F3.boolean.opBoolean","COPY",FACE,{"derivedFrom":makeQuery(id+"F3.opExtrude","CAP_FACE",FACE,{"disambiguationData":[OSD([subQ5,subQ1,subQ6,subQ7,subQ4,subQ3,subQ2,subQ0])],"isStart":false})})}),makeQuery(id+"F8.opExtrude","SWEPT_FACE",FACE,{"disambiguationData":[OSD([sQuery(id+"F7.wireOp",EDGE,"E67")])]})]});}
            var Q5;
            Q5=makeQuery(id+"F8.boolean.opBoolean","INTERSECT",EDGE,{"disambiguationData":[OD(0.0)],"derivedFrom":[makeQuery(id+"F5.opExtrude","SWEPT_FACE",FACE,{"disambiguationData":[OSD([sQuery(id+"F4.wireOp",EDGE,"E30")])]}),makeQuery(id+"F8.opExtrude","SWEPT_FACE",FACE,{"disambiguationData":[OSD([sQuery(id+"F7.wireOp",EDGE,"E67")])]})]});
            fillet(context, id + "F14", {"entities" : qUnion([Q0, Q1, Q2, Q3, Q4, Q5]), "radius" : 3 * mm, "tangentPropagation" : true, "allowEdgeOverflow" : false});
        }
        {
            var Q0;
            Q0=makeQuery(id+"F1.opExtrude","CAP_EDGE",EDGE,{"disambiguationData":[OSD([sQuery(id+"F0.wireOp",EDGE,"E1.bottom")])],"isStart":false});
            fillet(context, id + "F15", {"entities" : qUnion([Q0]), "radius" : 2 * mm, "tangentPropagation" : true, "allowEdgeOverflow" : false});
        }
        {
            var Q0;
            {var subQ0=sQuery(id+"F0.wireOp",EDGE,"E21.filletArc");var subQ1=sQuery(id+"F0.wireOp",EDGE,"E7");var subQ2=sQuery(id+"F0.wireOp",EDGE,"E6");var subQ3=sQuery(id+"F0.wireOp",EDGE,"E5");var subQ4=sQuery(id+"F0.wireOp",EDGE,"E4");var subQ5=sQuery(id+"F0.wireOp",EDGE,"E22.filletArc");var subQ6=sQuery(id+"F0.wireOp",EDGE,"E1.bottom");var subQ7=sQuery(id+"F0.wireOp",EDGE,"E1.right");var subQ8=sQuery(id+"F0.wireOp",EDGE,"E1.top");var subQ9=sQuery(id+"F0.wireOp",EDGE,"E1.left");var subQ10=sQuery(id+"F0.wireOp",EDGE,"E23.filletArc");var subQ11=sQuery(id+"F0.wireOp",EDGE,"E24.filletArc");Q0=makeQuery(id+"F2.boolean.opBoolean","SPLIT",FACE,{"disambiguationData":[TD([makeQuery(id+"F1.opExtrude","SWEPT_FACE",FACE,{"disambiguationData":[OSD([subQ6])]})])],"derivedFrom":makeQuery(id+"F1.opExtrude","CAP_FACE",FACE,{"disambiguationData":[OSD([subQ6,subQ8,subQ9,subQ7,subQ4,subQ3,subQ2,subQ1,subQ0,subQ5,subQ10,subQ11])],"isStart":true})});}
            var sketch = newSketch(context, id + "F16", { "sketchPlane" : qUnion([Q0])});
            skLineSegment(sketch, "E79.0", {"start": v(-70, 90) * mm, "end": v(70, 90) * mm});
            skArc(sketch, "E79.1", {"start": v(-70, 90) * mm, "mid": v(-77.07, 87.07) * mm, "end": v(-80, 80) * mm});
            skLineSegment(sketch, "E79.2", {"start": v(-80, -80) * mm, "end": v(-80, 80) * mm});
            skArc(sketch, "E79.3", {"start": v(80, 80) * mm, "mid": v(77.07, 87.07) * mm, "end": v(70, 90) * mm});
            skLineSegment(sketch, "E79.4", {"start": v(80, -80) * mm, "end": v(80, 80) * mm});
            skArc(sketch, "E79.5", {"start": v(-80, -80) * mm, "mid": v(-77.07, -87.07) * mm, "end": v(-70, -90) * mm});
            skLineSegment(sketch, "E79.6", {"start": v(-70, -90) * mm, "end": v(70, -90) * mm});
            skArc(sketch, "E79.7", {"start": v(70, -90) * mm, "mid": v(77.07, -87.07) * mm, "end": v(80, -80) * mm});
            skArc(sketch, "E79.9", {"start": v(56.15, 48.18) * mm, "mid": v(0, 67.5) * mm, "end": v(-56.15, 48.18) * mm});
            skLineSegment(sketch, "E79.10", {"start": v(60, 40.3) * mm, "end": v(60, -40.3) * mm});
            skArc(sketch, "E79.11", {"start": v(60, 40.3) * mm, "mid": v(58.99, 44.68) * mm, "end": v(56.15, 48.18) * mm});
            skArc(sketch, "E79.12", {"start": v(-56.15, 48.18) * mm, "mid": v(-58.99, 44.68) * mm, "end": v(-60, 40.3) * mm});
            skLineSegment(sketch, "E79.13", {"start": v(-60, 40.3) * mm, "end": v(-60, -40.3) * mm});
            skArc(sketch, "E79.14", {"start": v(-60, -40.3) * mm, "mid": v(-58.99, -44.68) * mm, "end": v(-56.15, -48.18) * mm});
            skArc(sketch, "E79.15", {"start": v(-56.15, -48.18) * mm, "mid": v(0, -67.5) * mm, "end": v(56.15, -48.18) * mm});
            skArc(sketch, "E79.16", {"start": v(56.15, -48.18) * mm, "mid": v(58.99, -44.68) * mm, "end": v(60, -40.3) * mm});
            skCircle(sketch, "E79.17", {"center": v(60, 67.5) * mm, "radius": 4 * mm});
            skCircle(sketch, "E79.18", {"center": v(-60, 67.5) * mm, "radius": 4 * mm});
            skCircle(sketch, "E79.19", {"center": v(-60, -67.5) * mm, "radius": 4 * mm});
            skCircle(sketch, "E79.20", {"center": v(60, -67.5) * mm, "radius": 4 * mm});
            skLineSegment(sketch, "E80", {"start": v(0, 90) * mm, "end": v(0, 120) * mm, "construction": true});
            skCircle(sketch, "E81", {"center": v(0, 120) * mm, "radius": 6 * mm});
            skArc(sketch, "E82", {"start": v(15, 120) * mm, "mid": v(0, 135) * mm, "end": v(-15, 120) * mm});
            skLineSegment(sketch, "E83", {"start": v(-15, 120) * mm, "end": v(-15, 108) * mm});
            skLineSegment(sketch, "E84", {"start": v(-15, 108) * mm, "end": v(-33, 90) * mm});
            skLineSegment(sketch, "E85", {"start": v(15, 120) * mm, "end": v(15, 108) * mm});
            skLineSegment(sketch, "E86", {"start": v(15, 108) * mm, "end": v(33, 90) * mm});
            skLineSegment(sketch, "E87", {"start": v(-80, 0) * mm, "end": v(80, 0) * mm, "construction": true});
            skLineSegment(sketch, "E88.MirrorCS", {"start": v(15, -120) * mm, "end": v(15, -108) * mm});
            skArc(sketch, "E89.MirrorCS", {"start": v(15, -120) * mm, "mid": v(0, -135) * mm, "end": v(-15, -120) * mm});
            skLineSegment(sketch, "E90.MirrorCS", {"start": v(-15, -108) * mm, "end": v(-33, -90) * mm});
            skLineSegment(sketch, "E91.MirrorCS", {"start": v(15, -108) * mm, "end": v(33, -90) * mm});
            skLineSegment(sketch, "E92.MirrorCS", {"start": v(0, -90) * mm, "end": v(0, -120) * mm, "construction": true});
            skLineSegment(sketch, "E93.MirrorCS", {"start": v(-15, -120) * mm, "end": v(-15, -108) * mm});
            skCircle(sketch, "E94.MirrorC", {"center": v(0, -120) * mm, "radius": 6 * mm});
            skSolve(sketch);
        }
        {
            var Q0;
            Q0 = qSketchRegion(id + "F16", true);
            var Q1;
            Q1=makeQuery(id+"F2.opExtrude","CAP_FACE",FACE,{"disambiguationData":[OSD([sQuery(id+"F0.wireOp",EDGE,"E12"),sQuery(id+"F0.wireOp",EDGE,"E13"),sQuery(id+"F0.wireOp",EDGE,"E14"),sQuery(id+"F0.wireOp",EDGE,"E15"),sQuery(id+"F0.wireOp",EDGE,"E17.filletArc"),sQuery(id+"F0.wireOp",EDGE,"E18.filletArc"),sQuery(id+"F0.wireOp",EDGE,"E19.filletArc"),sQuery(id+"F0.wireOp",EDGE,"E20.filletArc"),sQuery(id+"F0.wireOp",EDGE,"E25.0"),sQuery(id+"F0.wireOp",EDGE,"E25.1"),sQuery(id+"F0.wireOp",EDGE,"E25.2"),sQuery(id+"F0.wireOp",EDGE,"E25.3"),sQuery(id+"F0.wireOp",EDGE,"E25.4"),sQuery(id+"F0.wireOp",EDGE,"E25.5"),sQuery(id+"F0.wireOp",EDGE,"E25.6"),sQuery(id+"F0.wireOp",EDGE,"E25.7")])],"isStart":false});
            extrude(context, id + "F17", {"entities" : qUnion([Q0]), "endBound" : BoundingType.UP_TO_SURFACE, "endBoundEntityFace" : qUnion([Q1]), "depth" : 25 * mm});
        }
    });
